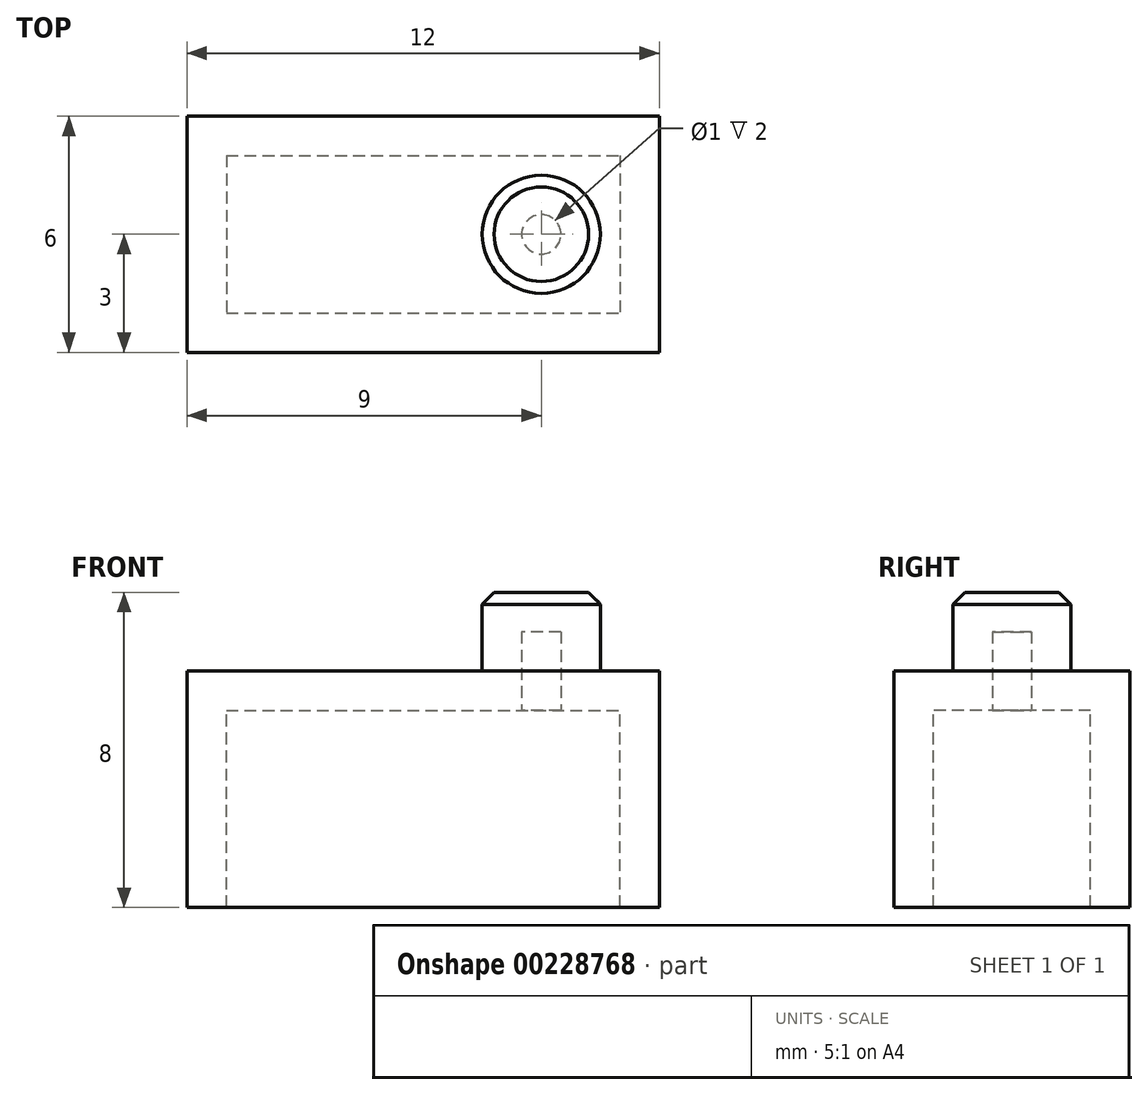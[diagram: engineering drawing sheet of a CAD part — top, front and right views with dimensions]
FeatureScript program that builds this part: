
annotation { "Feature Type Name" : "Feature", "Feature Type Description" : "" }
export const myFeature = defineFeature(function(context is Context, id is Id, definition is map)
    precondition{}
    {
        {
            var Q0;
            Q0=qCreatedBy(makeId("Top.planeOp"),FACE);
            var sketch = newSketch(context, id + "F3", { "sketchPlane" : qUnion([Q0])});
            skLineSegment(sketch, "E0.bottom", {"start": v(-6, 3) * mm, "end": v(6, 3) * mm});
            skLineSegment(sketch, "E0.top", {"start": v(-6, -3) * mm, "end": v(6, -3) * mm});
            skLineSegment(sketch, "E0.left", {"start": v(-6, 3) * mm, "end": v(-6, -3) * mm});
            skLineSegment(sketch, "E0.right", {"start": v(6, 3) * mm, "end": v(6, -3) * mm});
            skSolve(sketch);
        }
        {
            var Q0;
            Q0=makeQuery(id+"F3.imprint","IMPRINT",FACE,{"disambiguationData":[TD([[makeQuery(id+"F3.imprint","IMPRINT",EDGE,{"derivedFrom":sQuery(id+"F3.wireOp",EDGE,"E0.bottom")}),-1.0]])]});
            extrude(context, id + "F0", {"entities" : qUnion([Q0]), "oppositeDirection" : true, "depth" : 6 * mm});
        }
        {
            var Q0;
            Q0=qCreatedBy(makeId("Top.planeOp"),FACE);
            var sketch = newSketch(context, id + "F1", { "sketchPlane" : qUnion([Q0])});
            skCircle(sketch, "E1", {"center": v(3, 0) * mm, "radius": 1.5 * mm});
            skLineSegment(sketch, "E2", {"start": v(0, 3) * mm, "end": v(0, -3) * mm, "construction": true});
            skPoint(sketch, "E3.orphan", {"position": v(6, -3) * mm});
            skPoint(sketch, "E4.0.start.orphan", {"position": v(-6, -3) * mm});
            skCircle(sketch, "E5.MirrorC", {"center": v(-3, 0) * mm, "radius": 1.5 * mm});
            skSolve(sketch);
        }
        {
            var Q0;
            Q0=makeQuery(id+"F1.imprint","IMPRINT",FACE,{"disambiguationData":[TD([[makeQuery(id+"F1.imprint","IMPRINT",EDGE,{"derivedFrom":sQuery(id+"F1.wireOp",EDGE,"E1")}),1.0]])]});
            var Q1;
            Q1=makeQuery(id+"F1.imprint","IMPRINT",FACE,{"disambiguationData":[TD([[makeQuery(id+"F1.imprint","IMPRINT",EDGE,{"derivedFrom":sQuery(id+"F1.wireOp",EDGE,"E5.MirrorC")}),-1.0]])]});
            var Q2;
            Q2=sQuery(id+"F1.wireOp",EDGE,"E5.MirrorC");
            var Q3;
            Q3=sQuery(id+"F1.wireOp",EDGE,"E1");
            extrude(context, id + "F4", {"entities" : qUnion([Q0, Q1]), "operationType" : NewBodyOperationType.ADD, "surfaceEntities" : qUnion([Q2, Q3]), "depth" : 2 * mm});
        }
        {
            var Q0;
            Q0=makeQuery(id+"F4.opExtrude","CAP_EDGE",EDGE,{"disambiguationData":[OSD([sQuery(id+"F1.wireOp",EDGE,"E5.MirrorC")])],"isStart":false});
            var Q1;
            Q1=makeQuery(id+"F4.opExtrude","CAP_EDGE",EDGE,{"disambiguationData":[OSD([sQuery(id+"F1.wireOp",EDGE,"E1")])],"isStart":false});
            chamfer(context, id + "F5", {"entities" : qUnion([Q0, Q1]), "width" : 0.3 * mm, "tangentPropagation" : true});
        }
        {
            var Q0;
            Q0=makeQuery(id+"F0.opExtrude","CAP_FACE",FACE,{"disambiguationData":[OSD([sQuery(id+"F3.wireOp",EDGE,"E0.bottom"),sQuery(id+"F3.wireOp",EDGE,"E0.top"),sQuery(id+"F3.wireOp",EDGE,"E0.left"),sQuery(id+"F3.wireOp",EDGE,"E0.right")])],"isStart":false});
            shell(context, id + "F2", {"entities" : qUnion([Q0]), "thickness" : 1 * mm});
        }
    });
